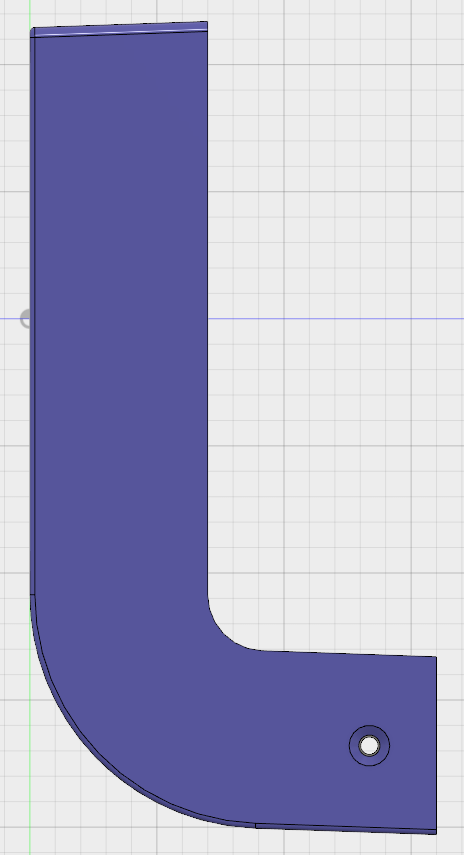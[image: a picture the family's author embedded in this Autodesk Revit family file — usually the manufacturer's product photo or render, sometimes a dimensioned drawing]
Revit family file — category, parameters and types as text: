
# Revit family: 0047951 Sylvania Lighting Fixture START eco Bollard L-Shape M IP54 570lm 830 BLK
name_source: partatom
category: Lighting Fixtures
revit_build: Autodesk Revit 2016 (Build: 20150220_1215(x64)
units: mm (PartAtom-declared; Revit-internal decimal feet)

## family parameters
Cut with Voids When Loaded = No
Host = Face
Light Source = Yes
OmniClass Number = 23.80.70.11.17
OmniClass Title = Specialized Lighting by Location or Use
Part Type = Normal
Room Calculation Point = No
Round Connector Dimension = Use Diameter
Shared = No

## types (1)
- START eco Bollard L-Shape M IP54 570lm 830 BLK
    Apparent Load = 8 VA
    Assembly Code = D5020200
    Body Material = Aluminum_Sylvania_Velite_Black
    Catalog Number = 0047951 START eco Bollard L-Shape M IP54 570lm 830 BLK
    Color Filter = 16777215
    Default Elevation = 0 mm  [stored 0 ft]
    Description = A range of sleek and stylish Outdoor LED luminaires.Velite is perfect for lighting courtyards, gardens and exterior entrances.Design  meets IK05 requirements.Available in various shapes, sizes and colours of die cast aluminium luminaires.Range includes bollards and various wall mounted direct and direct/indirect luminaires.High efficient thermal design: ta -20 to +45oC.High performance: delivers up to 830 lm (luminaire lumen output), and up to 71lm/W (total system efficiency).Available in warm white (3,000K).Energy class: A++, A+, A.Lifetime: 30,000 hours life at 70% of the original output L70.
    Diffuser Material = Polycarbonate_Sylvania_Velite_Clear
    Dimming Lamp Color Temperature Shift = <None>
    Drive Current = 300mA
    Electrical Protection = CLASS I
    Energy Class = A++ A+ A
    Height = 500 mm  [stored 1.64042 ft]
    IK Rating = IK05
    IP Rating = IP54
    Lamp = LED
    Lamp Comments = Integrated LED
    Length = 90 mm  [stored 0.295276 ft]
    Life = 25 000h
    Manufacturer = Feilo Sylvania
    Model = START eco Bollard L-Shape M IP54 570lm 830 BLK
    Photometric Web File = 0047951.ies
    Product Page URL = http://www.sylvania-lighting.com
    Ta Rating = -20°C to +45°C
    Tilt Angle = 90.00°
    URL = http://www.sylvania-lighting.com
    Voltage = 240 V
    Voltage Comments = UNV (Universal Voltage; 230-240 Volt)
    Weight = 1.54 kg
    Width = 35 mm  [stored 0.114829 ft]

note: [stored X ft] marks values corroborated as IEEE doubles in the binary element streams (Revit-internal decimal feet)

## geometry (parser evidence)
native form markers: Blend x5, Sweep x4
no freeform markers — native parametric forms only
